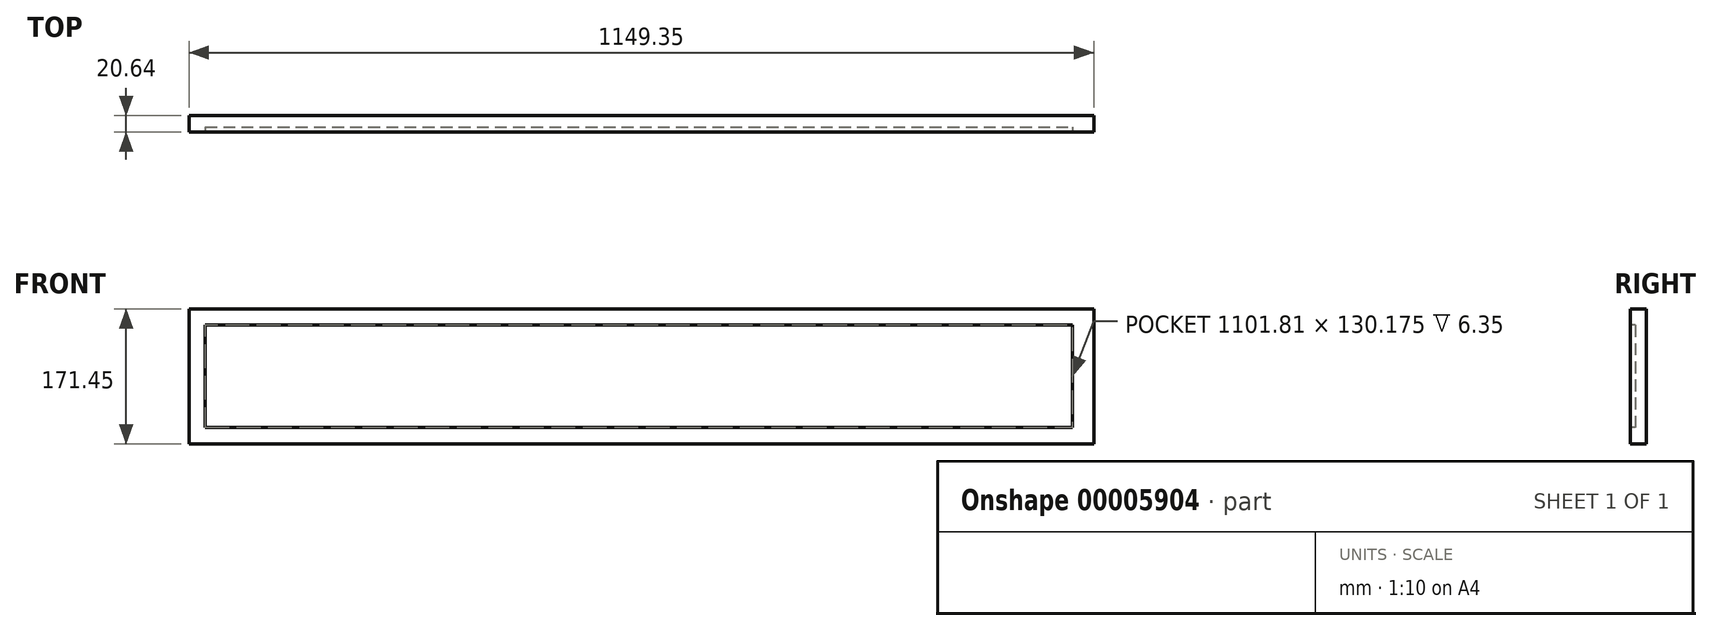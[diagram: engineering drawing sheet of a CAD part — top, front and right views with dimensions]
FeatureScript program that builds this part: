
annotation { "Feature Type Name" : "Feature", "Feature Type Description" : "" }
export const myFeature = defineFeature(function(context is Context, id is Id, definition is map)
    precondition{}
    {
        {
            var Q0;
            Q0=qCreatedBy(makeId("Front.planeOp"),FACE);
            var sketch = newSketch(context, id + "F0", { "sketchPlane" : qUnion([Q0])});
            skLineSegment(sketch, "E0.bottom", {"start": v(0, 0) * mm, "end": v(1149.35, 0) * mm});
            skLineSegment(sketch, "E0.top", {"start": v(0, 171.45) * mm, "end": v(1149.35, 171.45) * mm});
            skLineSegment(sketch, "E0.left", {"start": v(0, 0) * mm, "end": v(0, 171.45) * mm});
            skLineSegment(sketch, "E0.right", {"start": v(1149.35, 0) * mm, "end": v(1149.35, 171.45) * mm});
            skSolve(sketch);
        }
        {
            var Q0;
            Q0=makeQuery(id+"F0.imprint","IMPRINT",FACE,{"disambiguationData":[TD([[makeQuery(id+"F0.imprint","IMPRINT",EDGE,{"derivedFrom":sQuery(id+"F0.wireOp",EDGE,"E0.bottom")}),1.0]])]});
            extrude(context, id + "F1", {"entities" : qUnion([Q0]), "depth" : 20.64 * mm});
        }
        {
            var Q0;
            Q0=makeQuery(id+"F1.opExtrude","CAP_FACE",FACE,{"disambiguationData":[OSD([sQuery(id+"F0.wireOp",EDGE,"E0.bottom"),sQuery(id+"F0.wireOp",EDGE,"E0.top"),sQuery(id+"F0.wireOp",EDGE,"E0.left"),sQuery(id+"F0.wireOp",EDGE,"E0.right")])],"isStart":false});
            var sketch = newSketch(context, id + "F2", { "sketchPlane" : qUnion([Q0])});
            skLineSegment(sketch, "E1.bottom", {"start": v(20.64, 150.81) * mm, "end": v(1122.45, 150.81) * mm});
            skLineSegment(sketch, "E1.top", {"start": v(20.64, 20.64) * mm, "end": v(1122.45, 20.64) * mm});
            skLineSegment(sketch, "E1.left", {"start": v(20.64, 150.81) * mm, "end": v(20.64, 20.64) * mm});
            skLineSegment(sketch, "E1.right", {"start": v(1122.45, 150.81) * mm, "end": v(1122.45, 20.64) * mm});
            skLineSegment(sketch, "E2", {"start": v(129.65, 171.45) * mm, "end": v(129.65, 150.81) * mm, "construction": true});
            skLineSegment(sketch, "E3", {"start": v(0, 85.73) * mm, "end": v(20.64, 85.73) * mm, "construction": true});
            skLineSegment(sketch, "E4", {"start": v(135.8, 0) * mm, "end": v(135.8, 20.64) * mm, "construction": true});
            skLineSegment(sketch, "E5", {"start": v(1122.45, 89.66) * mm, "end": v(1149.35, 89.66) * mm, "construction": true});
            skSolve(sketch);
        }
        {
            var Q0;
            Q0=makeQuery(id+"F2.imprint","IMPRINT",FACE,{"disambiguationData":[TD([[makeQuery(id+"F2.imprint","IMPRINT",EDGE,{"derivedFrom":sQuery(id+"F2.wireOp",EDGE,"E1.bottom")}),-1.0]])]});
            extrude(context, id + "F3", {"entities" : qUnion([Q0]), "operationType" : NewBodyOperationType.REMOVE, "oppositeDirection" : true, "depth" : 6.35 * mm});
        }
    });
